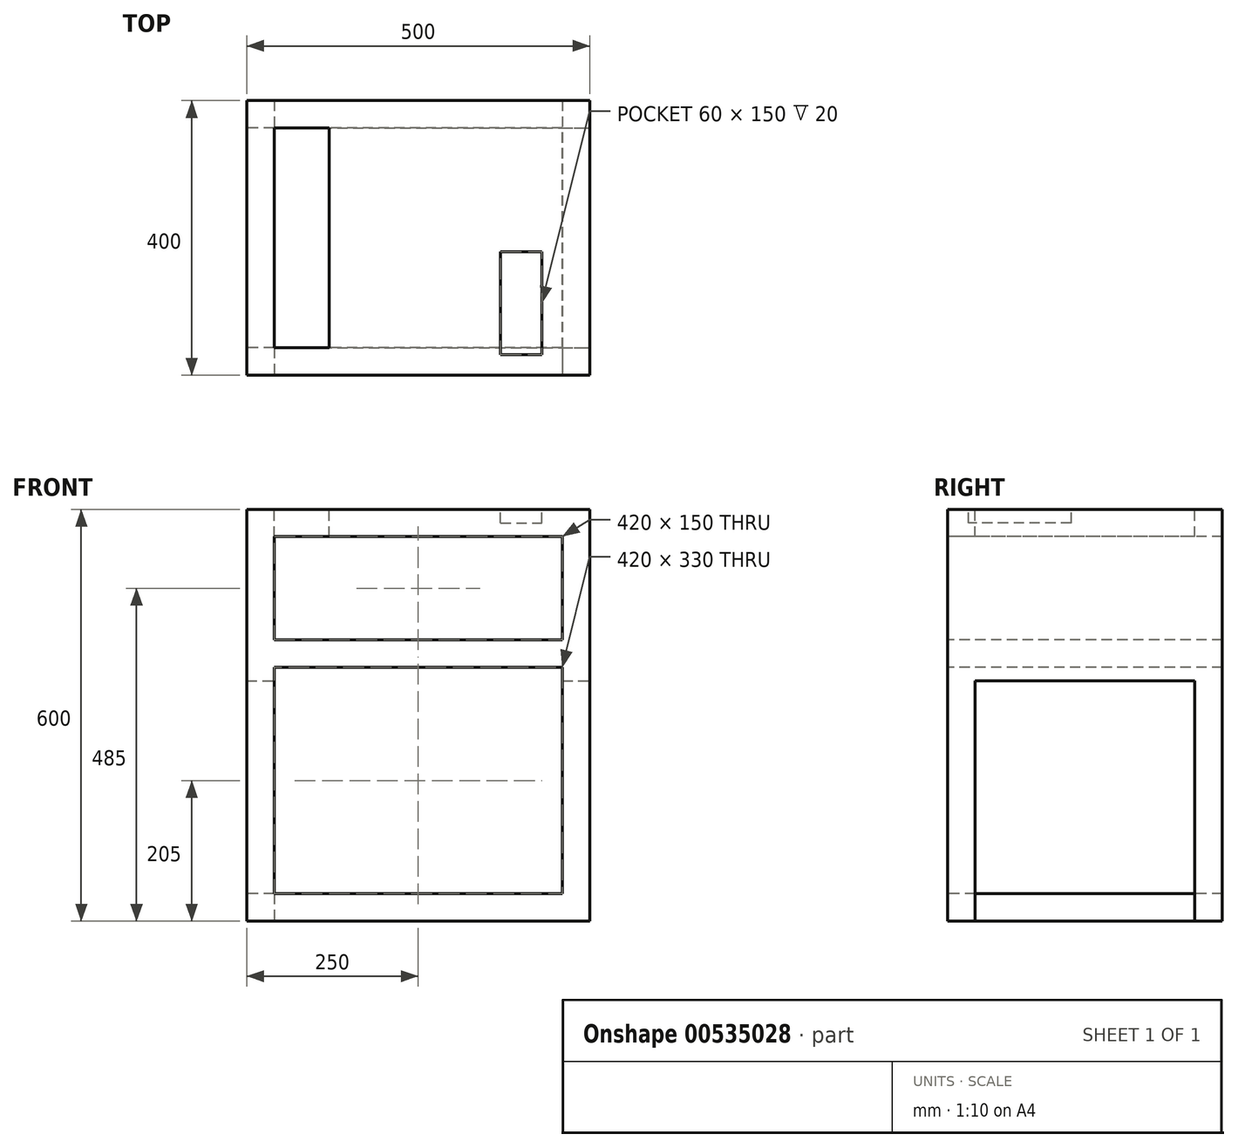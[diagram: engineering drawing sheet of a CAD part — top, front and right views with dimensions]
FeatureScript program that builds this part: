
annotation { "Feature Type Name" : "Feature", "Feature Type Description" : "" }
export const myFeature = defineFeature(function(context is Context, id is Id, definition is map)
    precondition{}
    {
        {
            var Q0;
            Q0=qCreatedBy(makeId("Front.planeOp"),FACE);
            var sketch = newSketch(context, id + "F0", { "sketchPlane" : qUnion([Q0])});
            skLineSegment(sketch, "E0.bottom", {"start": v(0, 0) * mm, "end": v(500, 0) * mm});
            skLineSegment(sketch, "E0.top", {"start": v(0, 600) * mm, "end": v(500, 600) * mm});
            skLineSegment(sketch, "E0.left", {"start": v(0, 0) * mm, "end": v(0, 600) * mm});
            skLineSegment(sketch, "E0.right", {"start": v(500, 0) * mm, "end": v(500, 600) * mm});
            skSolve(sketch);
        }
        {
            var Q0;
            Q0=makeQuery(id+"F0.imprint","IMPRINT",FACE,{"disambiguationData":[TD([[makeQuery(id+"F0.imprint","IMPRINT",EDGE,{"derivedFrom":sQuery(id+"F0.wireOp",EDGE,"E0.bottom")}),1.0]])]});
            extrude(context, id + "F1", {"entities" : qUnion([Q0]), "depth" : 400 * mm, "offsetDistance" : 25 * mm});
        }
        {
            var Q0;
            Q0=makeQuery(id+"F1.opExtrude","SWEPT_FACE",FACE,{"disambiguationData":[OSD([sQuery(id+"F0.wireOp",EDGE,"E0.top")])]});
            var sketch = newSketch(context, id + "F2", { "sketchPlane" : qUnion([Q0])});
            skSolve(sketch);
        }
        {
            var Q0;
            {var subQ0=sQuery(id+"F0.wireOp",EDGE,"E0.top");Q0=makeQuery(id+"F2.imprint","IMPRINT",FACE,{"disambiguationData":[TD([[makeQuery(id+"F2.imprint","IMPRINT",EDGE,{"derivedFrom":makeQuery(id+"F1.opExtrude","CAP_EDGE",EDGE,{"disambiguationData":[OSD([subQ0])],"isStart":true})}),-1.0]])]});}
            var sketch = newSketch(context, id + "F3", { "sketchPlane" : qUnion([Q0])});
            skLineSegment(sketch, "E1.bottom", {"start": v(120, -360) * mm, "end": v(40, -360) * mm});
            skLineSegment(sketch, "E1.top", {"start": v(120, -40) * mm, "end": v(40, -40) * mm});
            skLineSegment(sketch, "E1.left", {"start": v(120, -360) * mm, "end": v(120, -40) * mm});
            skLineSegment(sketch, "E1.right", {"start": v(40, -360) * mm, "end": v(40, -40) * mm});
            skPoint(sketch, "E1.middle", {"position": v(80, -200) * mm});
            skSolve(sketch);
        }
        {
            var Q0;
            Q0=makeQuery(id+"F3.imprint","IMPRINT",FACE,{"disambiguationData":[TD([[makeQuery(id+"F3.imprint","IMPRINT",EDGE,{"derivedFrom":sQuery(id+"F3.wireOp",EDGE,"E1.bottom")}),-1.0]])]});
            extrude(context, id + "F4", {"entities" : qUnion([Q0]), "operationType" : NewBodyOperationType.REMOVE, "oppositeDirection" : true, "depth" : 200 * mm, "offsetDistance" : 25 * mm});
        }
        {
            var Q0;
            Q0=makeQuery(id+"F1.opExtrude","CAP_FACE",FACE,{"disambiguationData":[OSD([sQuery(id+"F0.wireOp",EDGE,"E0.bottom"),sQuery(id+"F0.wireOp",EDGE,"E0.top"),sQuery(id+"F0.wireOp",EDGE,"E0.left"),sQuery(id+"F0.wireOp",EDGE,"E0.right")])],"isStart":false});
            var sketch = newSketch(context, id + "F5", { "sketchPlane" : qUnion([Q0])});
            skLineSegment(sketch, "E2.bottom", {"start": v(460, 40) * mm, "end": v(40, 40) * mm});
            skLineSegment(sketch, "E2.top", {"start": v(460, 560) * mm, "end": v(40, 560) * mm});
            skLineSegment(sketch, "E2.left", {"start": v(460, 40) * mm, "end": v(460, 560) * mm});
            skLineSegment(sketch, "E2.right", {"start": v(40, 40) * mm, "end": v(40, 560) * mm});
            skPoint(sketch, "E2.middle", {"position": v(250, 300) * mm});
            skPoint(sketch, "E2.middle.positionSnap0", {"position": v(0, 300) * mm});
            skPoint(sketch, "E2.middle.positionSnap1", {"position": v(250, 600) * mm});
            skPoint(sketch, "E2.centerSnap0", {"position": v(0, 300) * mm});
            skPoint(sketch, "E2.centerSnap1", {"position": v(250, 600) * mm});
            skSolve(sketch);
        }
        {
            var Q0;
            Q0=makeQuery(id+"F5.imprint","IMPRINT",FACE,{"disambiguationData":[TD([[makeQuery(id+"F5.imprint","IMPRINT",EDGE,{"derivedFrom":sQuery(id+"F5.wireOp",EDGE,"E2.bottom")}),-1.0]])]});
            extrude(context, id + "F6", {"entities" : qUnion([Q0]), "operationType" : NewBodyOperationType.REMOVE, "oppositeDirection" : true, "depth" : 400 * mm, "offsetDistance" : 25 * mm});
        }
        {
            var Q0;
            Q0=makeQuery(id+"F6.boolean.opBoolean","COPY",FACE,{"derivedFrom":makeQuery(id+"F6.opExtrude","SWEPT_FACE",FACE,{"disambiguationData":[OSD([sQuery(id+"F5.wireOp",EDGE,"E2.left")])]})});
            var sketch = newSketch(context, id + "F7", { "sketchPlane" : qUnion([Q0])});
            skLineSegment(sketch, "E3.bottom", {"start": v(0, 410) * mm, "end": v(400, 410) * mm});
            skLineSegment(sketch, "E3.top", {"start": v(0, 370) * mm, "end": v(400, 370) * mm});
            skLineSegment(sketch, "E3.left", {"start": v(0, 410) * mm, "end": v(0, 370) * mm});
            skLineSegment(sketch, "E3.right", {"start": v(400, 410) * mm, "end": v(400, 370) * mm});
            skSolve(sketch);
        }
        {
            var Q0;
            Q0=makeQuery(id+"F7.imprint","IMPRINT",FACE,{"disambiguationData":[TD([[makeQuery(id+"F7.imprint","IMPRINT",EDGE,{"derivedFrom":sQuery(id+"F7.wireOp",EDGE,"E3.bottom")}),-1.0]])]});
            extrude(context, id + "F8", {"entities" : qUnion([Q0]), "operationType" : NewBodyOperationType.ADD, "depth" : 420 * mm, "offsetDistance" : 25 * mm});
        }
        {
            var Q0;
            {var subQ0=sQuery(id+"F0.wireOp",EDGE,"E0.top");Q0=makeQuery(id+"F2.imprint","IMPRINT",FACE,{"disambiguationData":[TD([[makeQuery(id+"F2.imprint","IMPRINT",EDGE,{"derivedFrom":makeQuery(id+"F1.opExtrude","CAP_EDGE",EDGE,{"disambiguationData":[OSD([subQ0])],"isStart":true})}),-1.0]])]});}
            var sketch = newSketch(context, id + "F9", { "sketchPlane" : qUnion([Q0])});
            skLineSegment(sketch, "E4.bottom", {"start": v(370, -220) * mm, "end": v(430, -220) * mm});
            skLineSegment(sketch, "E4.top", {"start": v(370, -370) * mm, "end": v(430, -370) * mm});
            skLineSegment(sketch, "E4.left", {"start": v(370, -220) * mm, "end": v(370, -370) * mm});
            skLineSegment(sketch, "E4.right", {"start": v(430, -220) * mm, "end": v(430, -370) * mm});
            skSolve(sketch);
        }
        {
            var Q0;
            Q0=makeQuery(id+"F9.imprint","IMPRINT",FACE,{"disambiguationData":[TD([[makeQuery(id+"F9.imprint","IMPRINT",EDGE,{"derivedFrom":sQuery(id+"F9.wireOp",EDGE,"E4.bottom")}),-1.0]])]});
            extrude(context, id + "F10", {"entities" : qUnion([Q0]), "operationType" : NewBodyOperationType.REMOVE, "oppositeDirection" : true, "depth" : 20 * mm, "offsetDistance" : 25 * mm});
        }
        {
            var Q0;
            Q0=makeQuery(id+"F1.opExtrude","SWEPT_FACE",FACE,{"disambiguationData":[OSD([sQuery(id+"F0.wireOp",EDGE,"E0.right")])]});
            var sketch = newSketch(context, id + "F11", { "sketchPlane" : qUnion([Q0])});
            skLineSegment(sketch, "E5.bottom", {"start": v(-360, 0) * mm, "end": v(-40, 0) * mm});
            skLineSegment(sketch, "E5.top", {"start": v(-360, 350) * mm, "end": v(-40, 350) * mm});
            skLineSegment(sketch, "E5.left", {"start": v(-360, 0) * mm, "end": v(-360, 350) * mm});
            skLineSegment(sketch, "E5.right", {"start": v(-40, 0) * mm, "end": v(-40, 350) * mm});
            skSolve(sketch);
        }
        {
            var Q0;
            Q0=makeQuery(id+"F11.imprint","IMPRINT",FACE,{"disambiguationData":[TD([[makeQuery(id+"F11.imprint","IMPRINT",EDGE,{"derivedFrom":sQuery(id+"F11.wireOp",EDGE,"E5.bottom")}),1.0]])]});
            extrude(context, id + "F12", {"entities" : qUnion([Q0]), "operationType" : NewBodyOperationType.REMOVE, "oppositeDirection" : true, "depth" : 625 * mm, "offsetDistance" : 25 * mm});
        }
        {
            var Q0;
            Q0=makeQuery(id+"F12.boolean.opBoolean","COPY",FACE,{"derivedFrom":makeQuery(id+"F12.opExtrude","SWEPT_FACE",FACE,{"disambiguationData":[OSD([sQuery(id+"F11.wireOp",EDGE,"E5.right")])]})});
            var sketch = newSketch(context, id + "F13", { "sketchPlane" : qUnion([Q0])});
            skLineSegment(sketch, "E6.bottom", {"start": v(40, 40) * mm, "end": v(0, 40) * mm});
            skLineSegment(sketch, "E6.top", {"start": v(40, 0) * mm, "end": v(0, 0) * mm});
            skLineSegment(sketch, "E6.left", {"start": v(40, 40) * mm, "end": v(40, 0) * mm});
            skLineSegment(sketch, "E6.right", {"start": v(0, 40) * mm, "end": v(0, 0) * mm});
            skSolve(sketch);
        }
        {
            var Q0;
            Q0=makeQuery(id+"F13.imprint","IMPRINT",FACE,{"disambiguationData":[TD([[makeQuery(id+"F13.imprint","IMPRINT",EDGE,{"derivedFrom":sQuery(id+"F13.wireOp",EDGE,"E6.bottom")}),1.0]])]});
            extrude(context, id + "F14", {"entities" : qUnion([Q0]), "operationType" : NewBodyOperationType.ADD, "depth" : 325 * mm, "offsetDistance" : 25 * mm});
        }
    });
